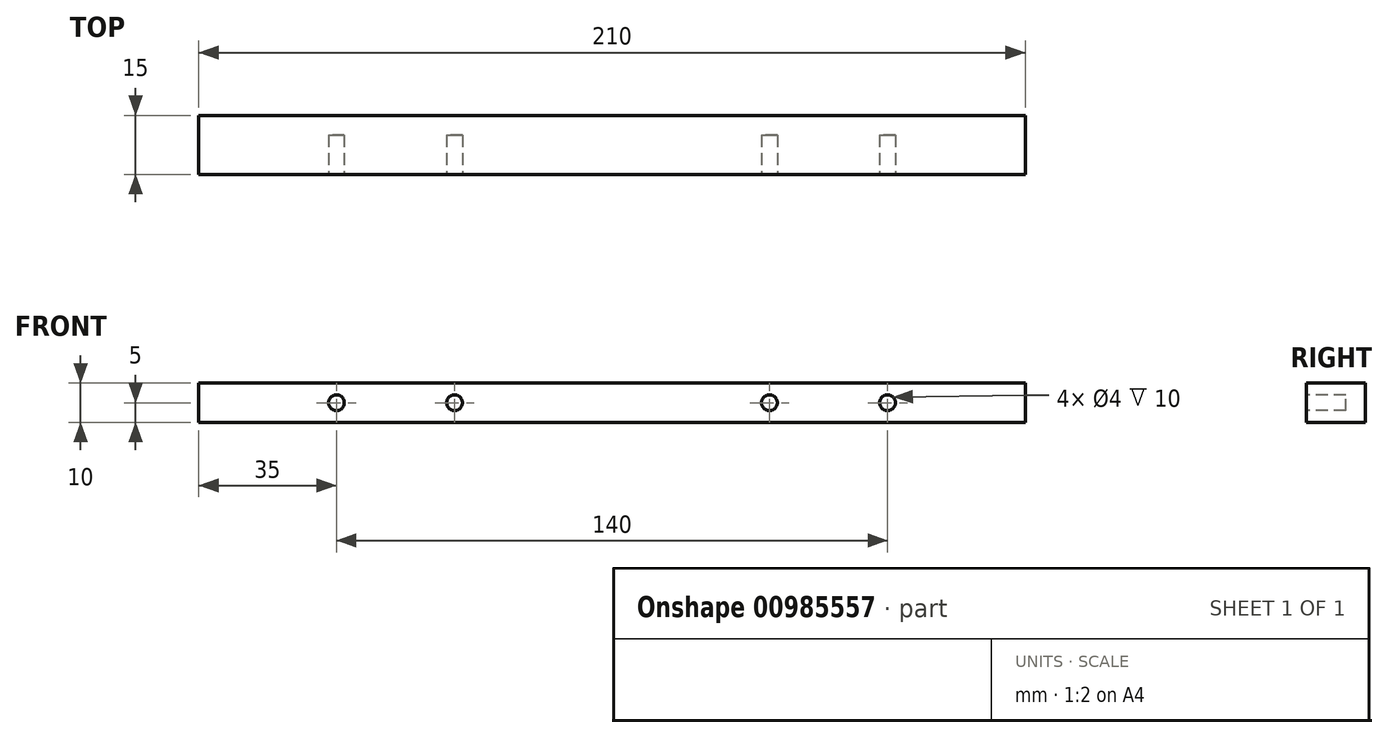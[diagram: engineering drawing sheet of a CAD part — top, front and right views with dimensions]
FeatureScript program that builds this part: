
annotation { "Feature Type Name" : "Feature", "Feature Type Description" : "" }
export const myFeature = defineFeature(function(context is Context, id is Id, definition is map)
    precondition{}
    {
        {
            var Q0;
            Q0=qCreatedBy(makeId("Top.planeOp"),FACE);
            var sketch = newSketch(context, id + "F0", { "sketchPlane" : qUnion([Q0])});
            skLineSegment(sketch, "E0.bottom", {"start": v(105, -7.5) * mm, "end": v(-105, -7.5) * mm});
            skLineSegment(sketch, "E0.top", {"start": v(105, 7.5) * mm, "end": v(-105, 7.5) * mm});
            skLineSegment(sketch, "E0.left", {"start": v(105, -7.5) * mm, "end": v(105, 7.5) * mm});
            skLineSegment(sketch, "E0.right", {"start": v(-105, -7.5) * mm, "end": v(-105, 7.5) * mm});
            skPoint(sketch, "E0.middle", {"position": v(0, 0) * mm});
            skSolve(sketch);
        }
        {
            var Q0;
            Q0=makeQuery(id+"F0.imprint","IMPRINT",FACE,{"disambiguationData":[TD([[makeQuery(id+"F0.imprint","IMPRINT",EDGE,{"derivedFrom":sQuery(id+"F0.wireOp",EDGE,"E0.bottom")}),-1.0]])]});
            extrude(context, id + "F1", {"entities" : qUnion([Q0]), "depth" : 10 * mm, "offsetDistance" : 25.4 * mm});
        }
        {
            var Q0;
            Q0=makeQuery(id+"F1.opExtrude","SWEPT_FACE",FACE,{"disambiguationData":[OSD([sQuery(id+"F0.wireOp",EDGE,"E0.bottom")])]});
            var sketch = newSketch(context, id + "F2", { "sketchPlane" : qUnion([Q0])});
            skLineSegment(sketch, "E1", {"start": v(82.51, 5) * mm, "end": v(-96.88, 5) * mm});
            skPoint(sketch, "E1.startSnap0", {"position": v(105, 5) * mm});
            skLineSegment(sketch, "E2", {"start": v(0, 30.57) * mm, "end": v(0, -40.25) * mm});
            skPoint(sketch, "E2.startSnap0", {"position": v(0, 10) * mm});
            skCircle(sketch, "E3", {"center": v(-70, 5) * mm, "radius": 2 * mm});
            skCircle(sketch, "E4", {"center": v(-40, 5) * mm, "radius": 2 * mm});
            skCircle(sketch, "E5", {"center": v(40, 5) * mm, "radius": 2 * mm});
            skCircle(sketch, "E6", {"center": v(70, 5) * mm, "radius": 2 * mm});
            skSolve(sketch);
        }
        {
            var Q0;
            {var subQ0=sQuery(id+"F2.wireOp",EDGE,"E3");var subQ1=sQuery(id+"F2.wireOp",EDGE,"E1");var subQ2=makeQuery(id+"F2.imprint","INTERSECT",VERTEX,{"disambiguationData":[OD(0.0)],"derivedFrom":[subQ1,subQ0]});Q0=makeQuery(id+"F2.imprint","IMPRINT",FACE,{"disambiguationData":[TD([[makeQuery(id+"F2.imprint","IMPRINT",EDGE,{"disambiguationData":[TD([[subQ2,-1.0]])],"derivedFrom":subQ1}),1.0]])]});}
            var Q1;
            {var subQ0=sQuery(id+"F2.wireOp",EDGE,"E3");var subQ1=sQuery(id+"F2.wireOp",EDGE,"E1");var subQ2=makeQuery(id+"F2.imprint","INTERSECT",VERTEX,{"disambiguationData":[OD(0.0)],"derivedFrom":[subQ1,subQ0]});Q1=makeQuery(id+"F2.imprint","IMPRINT",FACE,{"disambiguationData":[TD([[makeQuery(id+"F2.imprint","IMPRINT",EDGE,{"disambiguationData":[TD([[subQ2,-1.0]])],"derivedFrom":subQ1}),-1.0]])]});}
            var Q2;
            {var subQ0=sQuery(id+"F2.wireOp",EDGE,"E4");var subQ1=sQuery(id+"F2.wireOp",EDGE,"E1");var subQ2=makeQuery(id+"F2.imprint","INTERSECT",VERTEX,{"disambiguationData":[OD(0.0)],"derivedFrom":[subQ1,subQ0]});Q2=makeQuery(id+"F2.imprint","IMPRINT",FACE,{"disambiguationData":[TD([[makeQuery(id+"F2.imprint","IMPRINT",EDGE,{"disambiguationData":[TD([[subQ2,-1.0]])],"derivedFrom":subQ1}),-1.0]])]});}
            var Q3;
            {var subQ0=sQuery(id+"F2.wireOp",EDGE,"E4");var subQ1=sQuery(id+"F2.wireOp",EDGE,"E1");var subQ2=makeQuery(id+"F2.imprint","INTERSECT",VERTEX,{"disambiguationData":[OD(0.0)],"derivedFrom":[subQ1,subQ0]});Q3=makeQuery(id+"F2.imprint","IMPRINT",FACE,{"disambiguationData":[TD([[makeQuery(id+"F2.imprint","IMPRINT",EDGE,{"disambiguationData":[TD([[subQ2,-1.0]])],"derivedFrom":subQ1}),1.0]])]});}
            var Q4;
            {var subQ0=sQuery(id+"F2.wireOp",EDGE,"E5");var subQ1=sQuery(id+"F2.wireOp",EDGE,"E1");var subQ2=makeQuery(id+"F2.imprint","INTERSECT",VERTEX,{"disambiguationData":[OD(0.0)],"derivedFrom":[subQ1,subQ0]});Q4=makeQuery(id+"F2.imprint","IMPRINT",FACE,{"disambiguationData":[TD([[makeQuery(id+"F2.imprint","IMPRINT",EDGE,{"disambiguationData":[TD([[subQ2,-1.0]])],"derivedFrom":subQ1}),-1.0]])]});}
            var Q5;
            {var subQ0=sQuery(id+"F2.wireOp",EDGE,"E5");var subQ1=sQuery(id+"F2.wireOp",EDGE,"E1");var subQ2=makeQuery(id+"F2.imprint","INTERSECT",VERTEX,{"disambiguationData":[OD(0.0)],"derivedFrom":[subQ1,subQ0]});Q5=makeQuery(id+"F2.imprint","IMPRINT",FACE,{"disambiguationData":[TD([[makeQuery(id+"F2.imprint","IMPRINT",EDGE,{"disambiguationData":[TD([[subQ2,-1.0]])],"derivedFrom":subQ1}),1.0]])]});}
            var Q6;
            {var subQ0=sQuery(id+"F2.wireOp",EDGE,"E6");var subQ1=sQuery(id+"F2.wireOp",EDGE,"E1");var subQ2=makeQuery(id+"F2.imprint","INTERSECT",VERTEX,{"disambiguationData":[OD(0.0)],"derivedFrom":[subQ1,subQ0]});Q6=makeQuery(id+"F2.imprint","IMPRINT",FACE,{"disambiguationData":[TD([[makeQuery(id+"F2.imprint","IMPRINT",EDGE,{"disambiguationData":[TD([[subQ2,-1.0]])],"derivedFrom":subQ1}),-1.0]])]});}
            var Q7;
            {var subQ0=sQuery(id+"F2.wireOp",EDGE,"E6");var subQ1=sQuery(id+"F2.wireOp",EDGE,"E1");var subQ2=makeQuery(id+"F2.imprint","INTERSECT",VERTEX,{"disambiguationData":[OD(0.0)],"derivedFrom":[subQ1,subQ0]});Q7=makeQuery(id+"F2.imprint","IMPRINT",FACE,{"disambiguationData":[TD([[makeQuery(id+"F2.imprint","IMPRINT",EDGE,{"disambiguationData":[TD([[subQ2,-1.0]])],"derivedFrom":subQ1}),1.0]])]});}
            var Q8;
            {var subQ0=sQuery(id+"F2.wireOp",EDGE,"E5");var subQ1=sQuery(id+"F2.wireOp",EDGE,"E1");var subQ2=makeQuery(id+"F2.imprint","INTERSECT",VERTEX,{"disambiguationData":[OD(0.0)],"derivedFrom":[subQ1,subQ0]});Q8=makeQuery(id+"F2.imprint","IMPRINT",FACE,{"disambiguationData":[TD([[makeQuery(id+"F2.imprint","IMPRINT",EDGE,{"disambiguationData":[TD([[subQ2,1.0]])],"derivedFrom":subQ1}),-1.0]])]});}
            var Q9;
            {var subQ0=sQuery(id+"F2.wireOp",EDGE,"E5");var subQ1=sQuery(id+"F2.wireOp",EDGE,"E1");var subQ2=makeQuery(id+"F2.imprint","INTERSECT",VERTEX,{"disambiguationData":[OD(0.0)],"derivedFrom":[subQ1,subQ0]});Q9=makeQuery(id+"F2.imprint","IMPRINT",FACE,{"disambiguationData":[TD([[makeQuery(id+"F2.imprint","IMPRINT",EDGE,{"disambiguationData":[TD([[subQ2,1.0]])],"derivedFrom":subQ1}),1.0]])]});}
            var Q10;
            {var subQ0=sQuery(id+"F2.wireOp",EDGE,"E6");var subQ1=sQuery(id+"F2.wireOp",EDGE,"E1");var subQ2=makeQuery(id+"F2.imprint","INTERSECT",VERTEX,{"disambiguationData":[OD(0.0)],"derivedFrom":[subQ1,subQ0]});Q10=makeQuery(id+"F2.imprint","IMPRINT",FACE,{"disambiguationData":[TD([[makeQuery(id+"F2.imprint","IMPRINT",EDGE,{"disambiguationData":[TD([[subQ2,1.0]])],"derivedFrom":subQ1}),-1.0]])]});}
            var Q11;
            {var subQ0=sQuery(id+"F2.wireOp",EDGE,"E6");var subQ1=sQuery(id+"F2.wireOp",EDGE,"E1");var subQ2=makeQuery(id+"F2.imprint","INTERSECT",VERTEX,{"disambiguationData":[OD(0.0)],"derivedFrom":[subQ1,subQ0]});Q11=makeQuery(id+"F2.imprint","IMPRINT",FACE,{"disambiguationData":[TD([[makeQuery(id+"F2.imprint","IMPRINT",EDGE,{"disambiguationData":[TD([[subQ2,1.0]])],"derivedFrom":subQ1}),1.0]])]});}
            var Q12;
            {var subQ0=sQuery(id+"F2.wireOp",EDGE,"E4");var subQ1=sQuery(id+"F2.wireOp",EDGE,"E1");var subQ2=makeQuery(id+"F2.imprint","INTERSECT",VERTEX,{"disambiguationData":[OD(0.0)],"derivedFrom":[subQ1,subQ0]});Q12=makeQuery(id+"F2.imprint","IMPRINT",FACE,{"disambiguationData":[TD([[makeQuery(id+"F2.imprint","IMPRINT",EDGE,{"disambiguationData":[TD([[subQ2,1.0]])],"derivedFrom":subQ1}),-1.0]])]});}
            var Q13;
            {var subQ0=sQuery(id+"F2.wireOp",EDGE,"E4");var subQ1=sQuery(id+"F2.wireOp",EDGE,"E1");var subQ2=makeQuery(id+"F2.imprint","INTERSECT",VERTEX,{"disambiguationData":[OD(0.0)],"derivedFrom":[subQ1,subQ0]});Q13=makeQuery(id+"F2.imprint","IMPRINT",FACE,{"disambiguationData":[TD([[makeQuery(id+"F2.imprint","IMPRINT",EDGE,{"disambiguationData":[TD([[subQ2,1.0]])],"derivedFrom":subQ1}),1.0]])]});}
            var Q14;
            {var subQ0=sQuery(id+"F2.wireOp",EDGE,"E3");var subQ1=sQuery(id+"F2.wireOp",EDGE,"E1");var subQ2=makeQuery(id+"F2.imprint","INTERSECT",VERTEX,{"disambiguationData":[OD(0.0)],"derivedFrom":[subQ1,subQ0]});Q14=makeQuery(id+"F2.imprint","IMPRINT",FACE,{"disambiguationData":[TD([[makeQuery(id+"F2.imprint","IMPRINT",EDGE,{"disambiguationData":[TD([[subQ2,1.0]])],"derivedFrom":subQ1}),-1.0]])]});}
            var Q15;
            {var subQ0=sQuery(id+"F2.wireOp",EDGE,"E3");var subQ1=sQuery(id+"F2.wireOp",EDGE,"E1");var subQ2=makeQuery(id+"F2.imprint","INTERSECT",VERTEX,{"disambiguationData":[OD(0.0)],"derivedFrom":[subQ1,subQ0]});Q15=makeQuery(id+"F2.imprint","IMPRINT",FACE,{"disambiguationData":[TD([[makeQuery(id+"F2.imprint","IMPRINT",EDGE,{"disambiguationData":[TD([[subQ2,1.0]])],"derivedFrom":subQ1}),1.0]])]});}
            extrude(context, id + "F3", {"entities" : qUnion([Q0, Q1, Q2, Q3, Q4, Q5, Q6, Q7, Q8, Q9, Q10, Q11, Q12, Q13, Q14, Q15]), "operationType" : NewBodyOperationType.REMOVE, "oppositeDirection" : true, "depth" : 10 * mm, "offsetDistance" : 25.4 * mm});
        }
    });
